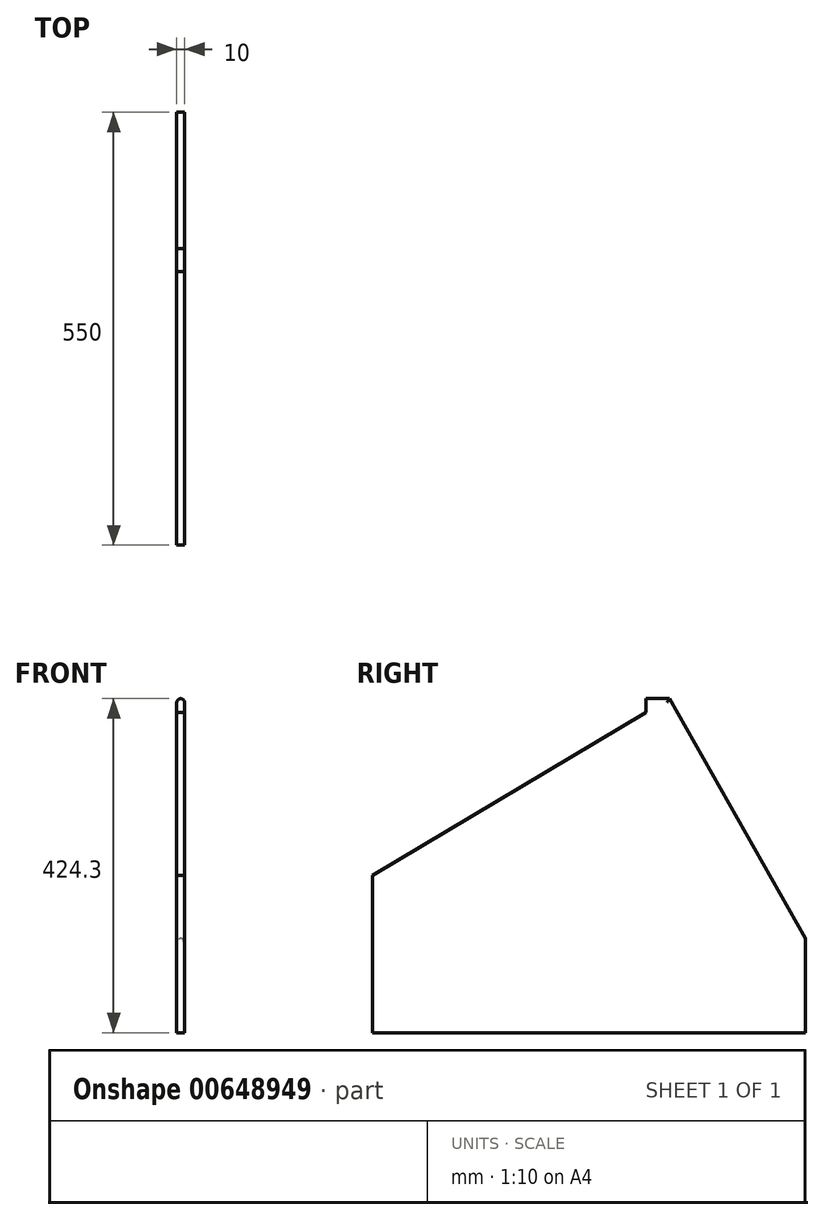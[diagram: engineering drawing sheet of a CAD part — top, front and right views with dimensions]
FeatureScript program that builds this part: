
annotation { "Feature Type Name" : "Feature", "Feature Type Description" : "" }
export const myFeature = defineFeature(function(context is Context, id is Id, definition is map)
    precondition{}
    {
        {
            var Q0;
            Q0=qCreatedBy(makeId("Right.planeOp"),FACE);
            var sketch = newSketch(context, id + "F0", { "sketchPlane" : qUnion([Q0])});
            skLineSegment(sketch, "E0", {"start": v(268.77, -74.31) * mm, "end": v(-281.23, -74.31) * mm});
            skLineSegment(sketch, "E1.bottom", {"start": v(-281.23, -74.31) * mm, "end": v(-174.2, -74.31) * mm});
            skLineSegment(sketch, "E1.top", {"start": v(-281.23, 125.69) * mm, "end": v(-174.2, 125.69) * mm});
            skLineSegment(sketch, "E1.left", {"start": v(-281.23, -74.31) * mm, "end": v(-281.23, 125.69) * mm});
            skLineSegment(sketch, "E1.right", {"start": v(-174.2, -74.31) * mm, "end": v(-174.2, 125.69) * mm});
            skLineSegment(sketch, "E2.bottom", {"start": v(268.77, -74.31) * mm, "end": v(155.05, -74.31) * mm});
            skLineSegment(sketch, "E2.top", {"start": v(268.77, 45.69) * mm, "end": v(155.05, 45.69) * mm});
            skLineSegment(sketch, "E2.left", {"start": v(268.77, -74.31) * mm, "end": v(268.77, 45.69) * mm});
            skLineSegment(sketch, "E2.right", {"start": v(155.05, -74.31) * mm, "end": v(155.05, 45.69) * mm});
            skLineSegment(sketch, "E3.bottom", {"start": v(66.1, -74.31) * mm, "end": v(95.85, -74.31) * mm});
            skLineSegment(sketch, "E3.top", {"start": v(66.1, 350) * mm, "end": v(95.85, 350) * mm});
            skLineSegment(sketch, "E3.left", {"start": v(66.1, -74.31) * mm, "end": v(66.1, 350) * mm});
            skLineSegment(sketch, "E3.right", {"start": v(95.85, -74.31) * mm, "end": v(95.85, 350) * mm});
            skLineSegment(sketch, "E4", {"start": v(268.77, 45.69) * mm, "end": v(95.85, 350) * mm});
            skLineSegment(sketch, "E5", {"start": v(95.85, 350) * mm, "end": v(-281.23, 125.69) * mm});
            skSolve(sketch);
        }
        {
            var Q0;
            Q0=qSketchRegion(id+"F0",true);
            extrude(context, id + "F1", {"entities" : qUnion([Q0]), "depth" : 10 * mm, "offsetDistance" : 25 * mm});
        }
        {
            var Q0;
            Q0=makeQuery(id+"F1.opExtrude","CAP_EDGE",EDGE,{"disambiguationData":[OSD([sQuery(id+"F0.wireOp",EDGE,"E4")])],"isStart":false});
            var Q1;
            Q1=makeQuery(id+"F1.opExtrude","CAP_EDGE",EDGE,{"disambiguationData":[OSD([sQuery(id+"F0.wireOp",EDGE,"E4")])],"isStart":true});
            var Q2;
            Q2=makeQuery(id+"F1.opExtrude","CAP_EDGE",EDGE,{"disambiguationData":[OSD([sQuery(id+"F0.wireOp",EDGE,"E3.top")])],"isStart":false});
            var Q3;
            Q3=makeQuery(id+"F1.opExtrude","CAP_EDGE",EDGE,{"disambiguationData":[OSD([sQuery(id+"F0.wireOp",EDGE,"E3.top")])],"isStart":true});
            fillet(context, id + "F2", {"entities" : qUnion([Q0, Q1, Q2, Q3]), "radius" : 5 * mm, "tangentPropagation" : true, "allowEdgeOverflow" : false});
        }
    });
